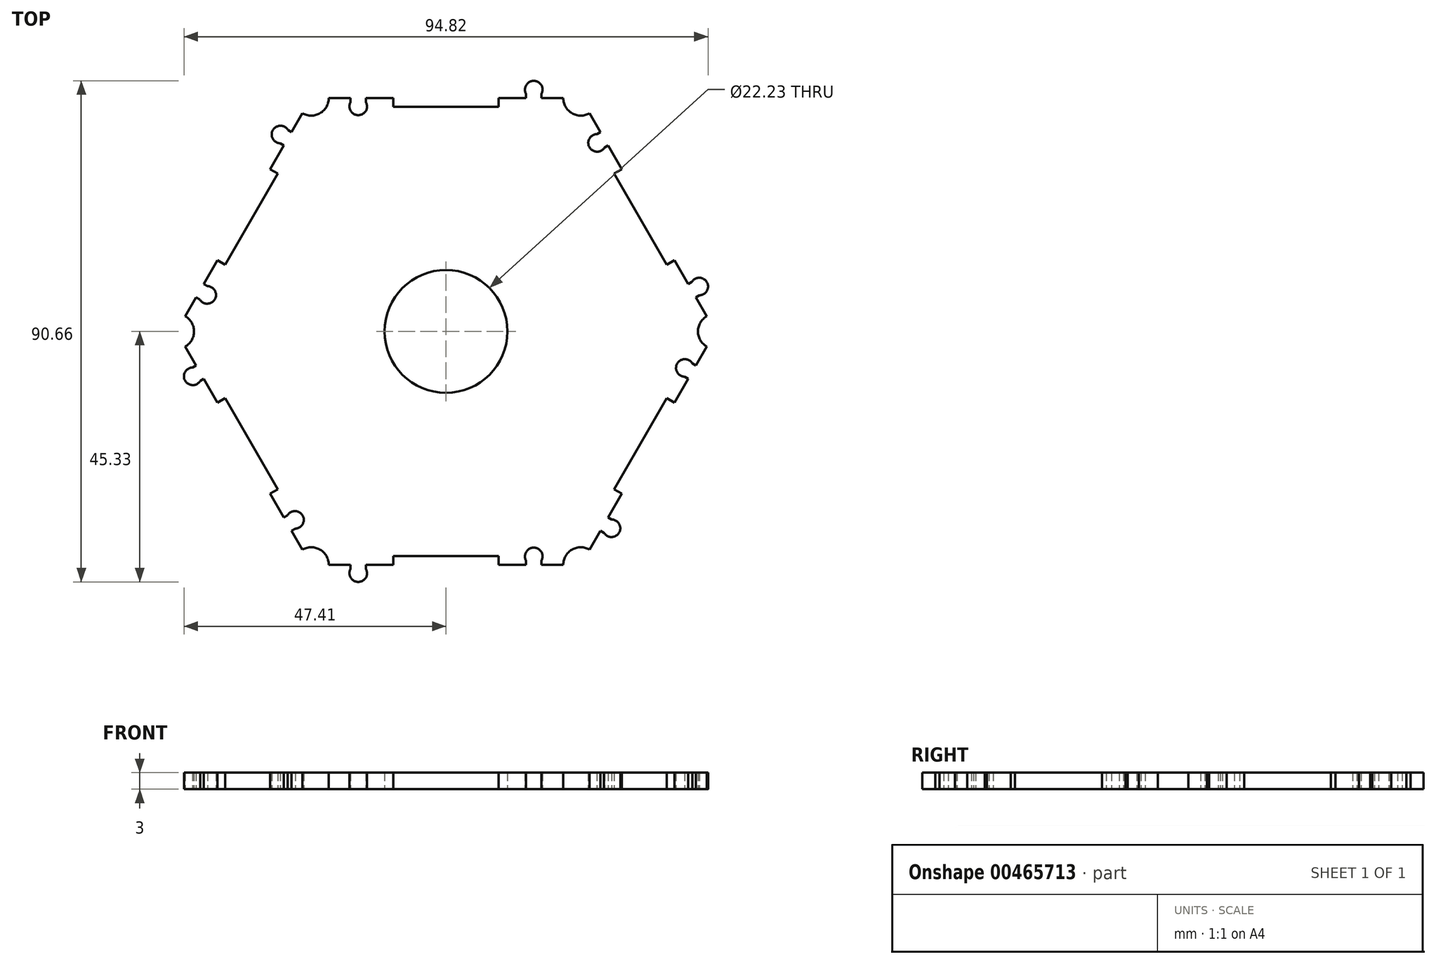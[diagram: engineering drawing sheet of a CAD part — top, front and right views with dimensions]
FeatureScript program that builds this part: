
annotation { "Feature Type Name" : "Feature", "Feature Type Description" : "" }
export const myFeature = defineFeature(function(context is Context, id is Id, definition is map)
    precondition{}
    {
        {
            var Q0;
            Q0=qCreatedBy(makeId("Top.planeOp"),FACE);
            var sketch = newSketch(context, id + "F0", { "sketchPlane" : qUnion([Q0])});
            skCircle(sketch, "E0.cCircle", {"center": v(0, 0) * mm, "radius": 42.23 * mm, "construction": true});
            skLineSegment(sketch, "E0.0", {"start": v(-48.76, 0) * mm, "end": v(-24.38, 42.23) * mm});
            skLineSegment(sketch, "E0.1", {"start": v(-24.38, 42.23) * mm, "end": v(24.38, 42.23) * mm});
            skLineSegment(sketch, "E0.2", {"start": v(24.38, 42.23) * mm, "end": v(48.76, 0) * mm});
            skLineSegment(sketch, "E0.3", {"start": v(48.76, 0) * mm, "end": v(24.38, -42.23) * mm});
            skLineSegment(sketch, "E0.4", {"start": v(24.38, -42.23) * mm, "end": v(-24.38, -42.23) * mm});
            skLineSegment(sketch, "E0.5", {"start": v(-24.38, -42.23) * mm, "end": v(-48.76, 0) * mm});
            skPoint(sketch, "E0.0.midPoint", {"position": v(-36.57, 21.11) * mm});
            skSolve(sketch);
        }
        {
            var Q0;
            Q0 = qSketchRegion(id + "F0", true);
            extrude(context, id + "F1", {"entities" : qUnion([Q0]), "depth" : 3 * mm});
        }
        {
            var Q0;
            Q0=qCreatedBy(makeId("Top.planeOp"),FACE);
            var sketch = newSketch(context, id + "F2", { "sketchPlane" : qUnion([Q0])});
            skLineSegment(sketch, "E1", {"start": v(-9.53, 42.23) * mm, "end": v(-9.53, 40.64) * mm});
            skLineSegment(sketch, "E2", {"start": v(-9.53, 40.64) * mm, "end": v(9.53, 40.64) * mm});
            skLineSegment(sketch, "E3", {"start": v(9.52, 40.64) * mm, "end": v(9.52, 42.23) * mm});
            skLineSegment(sketch, "E4", {"start": v(0, 40.64) * mm, "end": v(0, 42.48) * mm, "construction": true});
            skLineSegment(sketch, "E5", {"start": v(-9.53, 42.23) * mm, "end": v(9.53, 42.23) * mm});
            skArc(sketch, "E6", {"start": v(-17.27, 41.47) * mm, "mid": v(-15.88, 39.12) * mm, "end": v(-14.48, 41.47) * mm});
            skLineSegment(sketch, "E7", {"start": v(-17.27, 41.47) * mm, "end": v(-17.27, 42.23) * mm});
            skLineSegment(sketch, "E8", {"start": v(-17.27, 42.23) * mm, "end": v(-14.48, 42.23) * mm});
            skLineSegment(sketch, "E9", {"start": v(-14.48, 42.23) * mm, "end": v(-14.48, 41.47) * mm});
            skArc(sketch, "E10", {"start": v(-25.97, 39.48) * mm, "mid": v(-22.8, 39.48) * mm, "end": v(-21.2, 42.23) * mm});
            skLineSegment(sketch, "E11", {"start": v(-25.97, 39.48) * mm, "end": v(-24.38, 42.23) * mm});
            skLineSegment(sketch, "E12", {"start": v(-24.38, 42.23) * mm, "end": v(-21.2, 42.23) * mm});
            skLineSegment(sketch, "E13.1.0", {"start": v(-41.33, 12.86) * mm, "end": v(-31.8, 29.36) * mm});
            skLineSegment(sketch, "E13.1.1", {"start": v(-39.96, 12.07) * mm, "end": v(-30.43, 28.57) * mm});
            skArc(sketch, "E13.1.2", {"start": v(-47.17, -2.75) * mm, "mid": v(-45.59, 0) * mm, "end": v(-47.17, 2.75) * mm});
            skLineSegment(sketch, "E13.1.3", {"start": v(-35.2, 20.32) * mm, "end": v(-36.8, 21.24) * mm, "construction": true});
            skLineSegment(sketch, "E13.1.4", {"start": v(-48.76, 0) * mm, "end": v(-47.17, 2.75) * mm});
            skLineSegment(sketch, "E13.1.5", {"start": v(-47.17, -2.75) * mm, "end": v(-48.76, 0) * mm});
            skArc(sketch, "E13.1.6", {"start": v(-44.55, 5.77) * mm, "mid": v(-41.82, 5.81) * mm, "end": v(-43.15, 8.2) * mm});
            skLineSegment(sketch, "E13.1.7", {"start": v(-30.43, 28.57) * mm, "end": v(-31.8, 29.36) * mm});
            skLineSegment(sketch, "E13.1.8", {"start": v(-43.8, 8.58) * mm, "end": v(-43.15, 8.2) * mm});
            skLineSegment(sketch, "E13.1.9", {"start": v(-41.33, 12.86) * mm, "end": v(-39.96, 12.07) * mm});
            skLineSegment(sketch, "E13.1.10", {"start": v(-44.55, 5.77) * mm, "end": v(-45.2, 6.16) * mm});
            skLineSegment(sketch, "E13.1.11", {"start": v(-45.2, 6.16) * mm, "end": v(-43.8, 8.58) * mm});
            skLineSegment(sketch, "E13.2.0", {"start": v(-31.8, -29.36) * mm, "end": v(-41.33, -12.86) * mm});
            skLineSegment(sketch, "E13.2.1", {"start": v(-30.43, -28.57) * mm, "end": v(-39.96, -12.07) * mm});
            skArc(sketch, "E13.2.2", {"start": v(-21.2, -42.23) * mm, "mid": v(-22.8, -39.48) * mm, "end": v(-25.97, -39.48) * mm});
            skLineSegment(sketch, "E13.2.3", {"start": v(-35.2, -20.32) * mm, "end": v(-36.8, -21.24) * mm, "construction": true});
            skLineSegment(sketch, "E13.2.4", {"start": v(-24.38, -42.23) * mm, "end": v(-25.97, -39.48) * mm});
            skLineSegment(sketch, "E13.2.5", {"start": v(-21.2, -42.23) * mm, "end": v(-24.38, -42.23) * mm});
            skArc(sketch, "E13.2.6", {"start": v(-27.27, -35.7) * mm, "mid": v(-25.94, -33.31) * mm, "end": v(-28.67, -33.27) * mm});
            skLineSegment(sketch, "E13.2.7", {"start": v(-39.96, -12.07) * mm, "end": v(-41.33, -12.86) * mm});
            skLineSegment(sketch, "E13.2.8", {"start": v(-29.33, -33.65) * mm, "end": v(-28.67, -33.27) * mm});
            skLineSegment(sketch, "E13.2.9", {"start": v(-31.8, -29.36) * mm, "end": v(-30.43, -28.57) * mm});
            skLineSegment(sketch, "E13.2.10", {"start": v(-27.27, -35.7) * mm, "end": v(-27.93, -36.07) * mm});
            skLineSegment(sketch, "E13.2.11", {"start": v(-27.93, -36.07) * mm, "end": v(-29.33, -33.65) * mm});
            skLineSegment(sketch, "E13.3.0", {"start": v(9.52, -42.23) * mm, "end": v(-9.53, -42.23) * mm});
            skLineSegment(sketch, "E13.3.1", {"start": v(9.53, -40.64) * mm, "end": v(-9.53, -40.64) * mm});
            skArc(sketch, "E13.3.2", {"start": v(25.97, -39.48) * mm, "mid": v(22.8, -39.48) * mm, "end": v(21.2, -42.23) * mm});
            skLineSegment(sketch, "E13.3.3", {"start": v(0, -40.64) * mm, "end": v(0, -42.48) * mm, "construction": true});
            skLineSegment(sketch, "E13.3.4", {"start": v(24.38, -42.23) * mm, "end": v(21.2, -42.23) * mm});
            skLineSegment(sketch, "E13.3.5", {"start": v(25.97, -39.48) * mm, "end": v(24.38, -42.23) * mm});
            skArc(sketch, "E13.3.6", {"start": v(17.27, -41.47) * mm, "mid": v(15.88, -39.12) * mm, "end": v(14.48, -41.47) * mm});
            skLineSegment(sketch, "E13.3.7", {"start": v(-9.53, -40.64) * mm, "end": v(-9.53, -42.23) * mm});
            skLineSegment(sketch, "E13.3.8", {"start": v(14.48, -42.23) * mm, "end": v(14.48, -41.47) * mm});
            skLineSegment(sketch, "E13.3.9", {"start": v(9.52, -42.23) * mm, "end": v(9.52, -40.64) * mm});
            skLineSegment(sketch, "E13.3.10", {"start": v(17.27, -41.47) * mm, "end": v(17.27, -42.23) * mm});
            skLineSegment(sketch, "E13.3.11", {"start": v(17.27, -42.23) * mm, "end": v(14.48, -42.23) * mm});
            skLineSegment(sketch, "E13.4.0", {"start": v(41.33, -12.86) * mm, "end": v(31.8, -29.36) * mm});
            skLineSegment(sketch, "E13.4.1", {"start": v(39.96, -12.07) * mm, "end": v(30.43, -28.57) * mm});
            skArc(sketch, "E13.4.2", {"start": v(47.17, 2.75) * mm, "mid": v(45.59, 0) * mm, "end": v(47.17, -2.75) * mm});
            skLineSegment(sketch, "E13.4.3", {"start": v(35.2, -20.32) * mm, "end": v(36.8, -21.24) * mm, "construction": true});
            skLineSegment(sketch, "E13.4.4", {"start": v(48.76, 0) * mm, "end": v(47.17, -2.75) * mm});
            skLineSegment(sketch, "E13.4.5", {"start": v(47.17, 2.75) * mm, "end": v(48.76, 0) * mm});
            skArc(sketch, "E13.4.6", {"start": v(44.55, -5.77) * mm, "mid": v(41.82, -5.81) * mm, "end": v(43.15, -8.2) * mm});
            skLineSegment(sketch, "E13.4.7", {"start": v(30.43, -28.57) * mm, "end": v(31.8, -29.36) * mm});
            skLineSegment(sketch, "E13.4.8", {"start": v(43.8, -8.58) * mm, "end": v(43.15, -8.2) * mm});
            skLineSegment(sketch, "E13.4.9", {"start": v(41.33, -12.86) * mm, "end": v(39.96, -12.07) * mm});
            skLineSegment(sketch, "E13.4.10", {"start": v(44.55, -5.77) * mm, "end": v(45.2, -6.16) * mm});
            skLineSegment(sketch, "E13.4.11", {"start": v(45.2, -6.16) * mm, "end": v(43.8, -8.58) * mm});
            skLineSegment(sketch, "E13.5.0", {"start": v(31.8, 29.36) * mm, "end": v(41.33, 12.86) * mm});
            skLineSegment(sketch, "E13.5.1", {"start": v(30.43, 28.57) * mm, "end": v(39.96, 12.07) * mm});
            skArc(sketch, "E13.5.2", {"start": v(21.2, 42.23) * mm, "mid": v(22.8, 39.48) * mm, "end": v(25.97, 39.48) * mm});
            skLineSegment(sketch, "E13.5.3", {"start": v(35.2, 20.32) * mm, "end": v(36.8, 21.24) * mm, "construction": true});
            skLineSegment(sketch, "E13.5.4", {"start": v(24.38, 42.23) * mm, "end": v(25.97, 39.48) * mm});
            skLineSegment(sketch, "E13.5.5", {"start": v(21.2, 42.23) * mm, "end": v(24.38, 42.23) * mm});
            skArc(sketch, "E13.5.6", {"start": v(27.27, 35.7) * mm, "mid": v(25.94, 33.31) * mm, "end": v(28.67, 33.27) * mm});
            skLineSegment(sketch, "E13.5.7", {"start": v(39.96, 12.07) * mm, "end": v(41.33, 12.86) * mm});
            skLineSegment(sketch, "E13.5.8", {"start": v(29.33, 33.65) * mm, "end": v(28.67, 33.27) * mm});
            skLineSegment(sketch, "E13.5.9", {"start": v(31.8, 29.36) * mm, "end": v(30.43, 28.57) * mm});
            skLineSegment(sketch, "E13.5.10", {"start": v(27.27, 35.7) * mm, "end": v(27.93, 36.07) * mm});
            skLineSegment(sketch, "E13.5.11", {"start": v(27.93, 36.07) * mm, "end": v(29.33, 33.65) * mm});
            skPoint(sketch, "E13.center", {"position": v(0, 0) * mm});
            skCircle(sketch, "E14", {"center": v(0, 0) * mm, "radius": 11.11 * mm});
            skSolve(sketch);
        }
        {
            var Q0;
            Q0 = qSketchRegion(id + "F2", true);
            extrude(context, id + "F3", {"entities" : qUnion([Q0]), "operationType" : NewBodyOperationType.REMOVE, "endBound" : BoundingType.THROUGH_ALL, "depth" : 25.4 * mm});
        }
        {
            var Q0;
            Q0=qCreatedBy(makeId("Top.planeOp"),FACE);
            var sketch = newSketch(context, id + "F4", { "sketchPlane" : qUnion([Q0])});
            skArc(sketch, "E15", {"start": v(17.27, 42.99) * mm, "mid": v(15.87, 45.33) * mm, "end": v(14.48, 42.99) * mm});
            skLineSegment(sketch, "E16", {"start": v(14.48, 42.99) * mm, "end": v(14.48, 42.23) * mm});
            skLineSegment(sketch, "E17", {"start": v(14.48, 42.23) * mm, "end": v(17.27, 42.23) * mm});
            skLineSegment(sketch, "E18", {"start": v(17.27, 42.23) * mm, "end": v(17.27, 42.99) * mm});
            skLineSegment(sketch, "E19.1.0", {"start": v(-29.33, 33.65) * mm, "end": v(-27.93, 36.07) * mm});
            skArc(sketch, "E19.1.1", {"start": v(-28.6, 36.45) * mm, "mid": v(-31.32, 36.41) * mm, "end": v(-30, 34.03) * mm});
            skLineSegment(sketch, "E19.1.2", {"start": v(-27.93, 36.07) * mm, "end": v(-28.6, 36.45) * mm});
            skLineSegment(sketch, "E19.1.3", {"start": v(-30, 34.03) * mm, "end": v(-29.33, 33.65) * mm});
            skLineSegment(sketch, "E19.2.0", {"start": v(-43.8, -8.58) * mm, "end": v(-45.2, -6.16) * mm});
            skArc(sketch, "E19.2.1", {"start": v(-45.87, -6.54) * mm, "mid": v(-47.2, -8.92) * mm, "end": v(-44.47, -8.96) * mm});
            skLineSegment(sketch, "E19.2.2", {"start": v(-45.2, -6.16) * mm, "end": v(-45.87, -6.54) * mm});
            skLineSegment(sketch, "E19.2.3", {"start": v(-44.47, -8.96) * mm, "end": v(-43.8, -8.58) * mm});
            skLineSegment(sketch, "E19.3.0", {"start": v(-14.48, -42.23) * mm, "end": v(-17.27, -42.23) * mm});
            skArc(sketch, "E19.3.1", {"start": v(-17.27, -42.99) * mm, "mid": v(-15.88, -45.33) * mm, "end": v(-14.48, -42.99) * mm});
            skLineSegment(sketch, "E19.3.2", {"start": v(-17.27, -42.23) * mm, "end": v(-17.27, -42.99) * mm});
            skLineSegment(sketch, "E19.3.3", {"start": v(-14.48, -42.99) * mm, "end": v(-14.48, -42.23) * mm});
            skLineSegment(sketch, "E19.4.0", {"start": v(29.33, -33.65) * mm, "end": v(27.93, -36.07) * mm});
            skArc(sketch, "E19.4.1", {"start": v(28.6, -36.45) * mm, "mid": v(31.32, -36.41) * mm, "end": v(30, -34.03) * mm});
            skLineSegment(sketch, "E19.4.2", {"start": v(27.93, -36.07) * mm, "end": v(28.6, -36.45) * mm});
            skLineSegment(sketch, "E19.4.3", {"start": v(30, -34.03) * mm, "end": v(29.33, -33.65) * mm});
            skLineSegment(sketch, "E19.5.0", {"start": v(43.8, 8.58) * mm, "end": v(45.2, 6.16) * mm});
            skArc(sketch, "E19.5.1", {"start": v(45.87, 6.54) * mm, "mid": v(47.2, 8.92) * mm, "end": v(44.47, 8.96) * mm});
            skLineSegment(sketch, "E19.5.2", {"start": v(45.2, 6.16) * mm, "end": v(45.87, 6.54) * mm});
            skLineSegment(sketch, "E19.5.3", {"start": v(44.47, 8.96) * mm, "end": v(43.8, 8.58) * mm});
            skPoint(sketch, "E19.center", {"position": v(0, 0) * mm});
            skSolve(sketch);
        }
        {
            var Q0;
            Q0 = qSketchRegion(id + "F4", true);
            var Q1;
            Q1=makeQuery(id+"F1.opExtrude","CAP_FACE",FACE,{"disambiguationData":[OSD([sQuery(id+"F0.wireOp",EDGE,"E0.0"),sQuery(id+"F0.wireOp",EDGE,"E0.1"),sQuery(id+"F0.wireOp",EDGE,"E0.2"),sQuery(id+"F0.wireOp",EDGE,"E0.3"),sQuery(id+"F0.wireOp",EDGE,"E0.4"),sQuery(id+"F0.wireOp",EDGE,"E0.5")])],"isStart":false});
            extrude(context, id + "F5", {"entities" : qUnion([Q0]), "operationType" : NewBodyOperationType.ADD, "endBound" : BoundingType.UP_TO_SURFACE, "endBoundEntityFace" : qUnion([Q1]), "depth" : 25.4 * mm});
        }
    });
